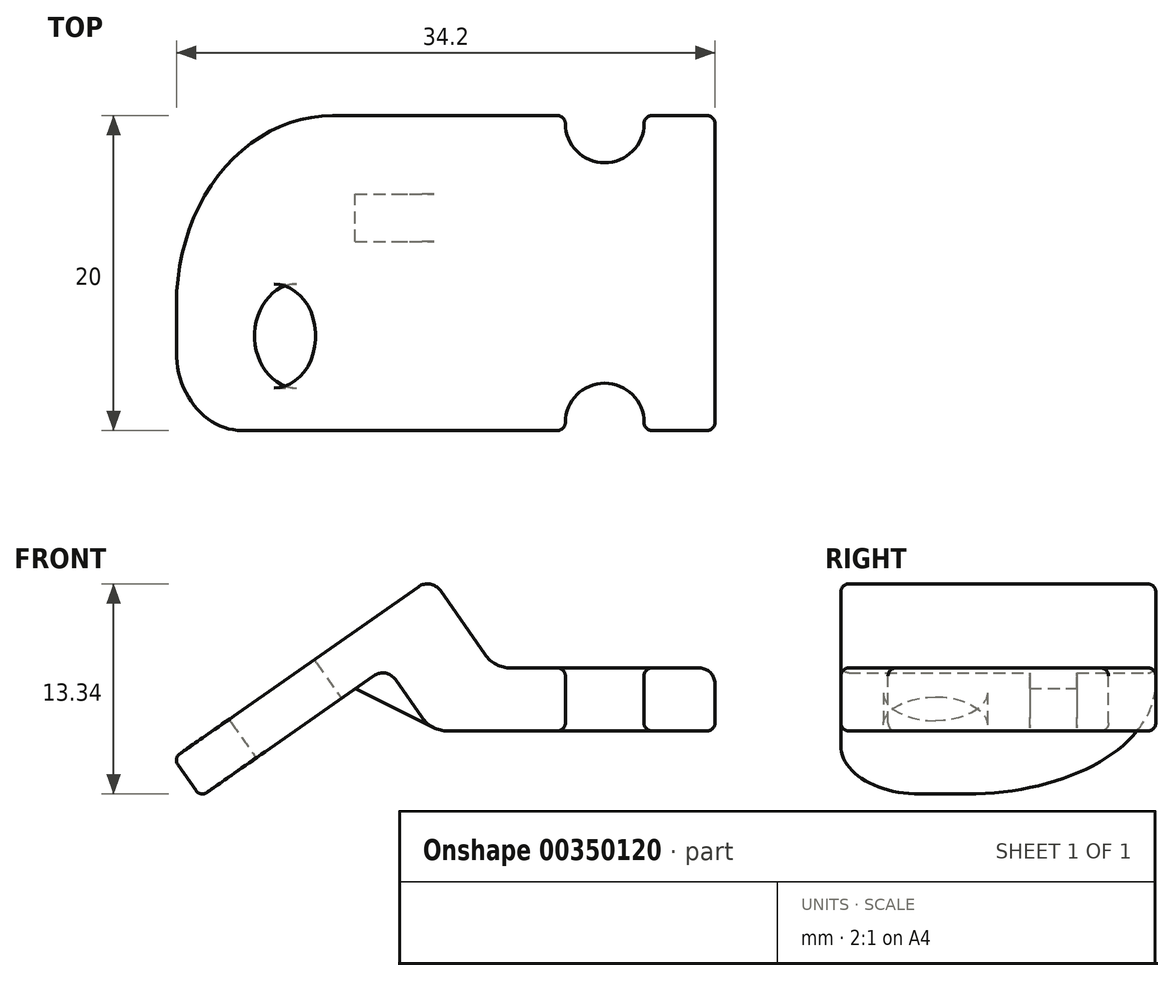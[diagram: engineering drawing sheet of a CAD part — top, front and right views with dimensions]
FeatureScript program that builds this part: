
annotation { "Feature Type Name" : "Feature", "Feature Type Description" : "" }
export const myFeature = defineFeature(function(context is Context, id is Id, definition is map)
    precondition{}
    {
        {
            var Q0;
            Q0=qCreatedBy(makeId("Front.planeOp"),FACE);
            var sketch = newSketch(context, id + "F0", { "sketchPlane" : qUnion([Q0])});
            skLineSegment(sketch, "E0", {"start": v(-18, 0) * mm, "end": v(0, 0) * mm});
            skLineSegment(sketch, "E1", {"start": v(0, 0) * mm, "end": v(0, 4) * mm});
            skLineSegment(sketch, "E2", {"start": v(0, 4) * mm, "end": v(-14, 4) * mm});
            skLineSegment(sketch, "E3", {"start": v(-14, 4) * mm, "end": v(-18.02, 9.73) * mm});
            skLineSegment(sketch, "E4", {"start": v(-18.02, 9.73) * mm, "end": v(-34.4, -1.74) * mm});
            skLineSegment(sketch, "E5", {"start": v(-34.4, -1.74) * mm, "end": v(-32.68, -4.2) * mm});
            skLineSegment(sketch, "E6", {"start": v(-32.68, -4.2) * mm, "end": v(-20.86, 4.08) * mm});
            skLineSegment(sketch, "E7", {"start": v(-18, 0) * mm, "end": v(-20.86, 4.08) * mm});
            skSolve(sketch);
        }
        {
            var Q0;
            Q0 = qSketchRegion(id + "F0", true);
            extrude(context, id + "F1", {"entities" : qUnion([Q0]), "depth" : 20 * mm});
        }
        {
            var Q0;
            Q0=makeQuery(id+"F1.opExtrude","SWEPT_FACE",FACE,{"disambiguationData":[OSD([sQuery(id+"F0.wireOp",EDGE,"E2")])]});
            var sketch = newSketch(context, id + "F2", { "sketchPlane" : qUnion([Q0])});
            skCircle(sketch, "E8", {"center": v(-7, -0.5) * mm, "radius": 2.5 * mm});
            skCircle(sketch, "E9", {"center": v(-7, -19.5) * mm, "radius": 2.5 * mm});
            skLineSegment(sketch, "E10", {"start": v(-14, -10) * mm, "end": v(0, -10) * mm, "construction": true});
            skLineSegment(sketch, "E11", {"start": v(-7, -10) * mm, "end": v(-7, -0.5) * mm, "construction": true});
            skLineSegment(sketch, "E12", {"start": v(-7, -10) * mm, "end": v(-7, -19.5) * mm, "construction": true});
            skSolve(sketch);
        }
        {
            var Q0;
            Q0 = qSketchRegion(id + "F2", true);
            extrude(context, id + "F3", {"entities" : qUnion([Q0]), "operationType" : NewBodyOperationType.REMOVE, "endBound" : BoundingType.THROUGH_ALL, "oppositeDirection" : true, "depth" : 25.4 * mm});
        }
        {
            var Q0;
            Q0=makeQuery(id+"F1.opExtrude","SWEPT_EDGE",EDGE,{"disambiguationData":[OSD([sQuery(id+"F0.wireOp",EDGE,"E6"),sQuery(id+"F0.wireOp",EDGE,"E7")])]});
            fillet(context, id + "F4", {"entities" : qUnion([Q0]), "radius" : 1 * mm, "tangentPropagation" : true, "allowEdgeOverflow" : false});
        }
        {
            var Q0;
            Q0=makeQuery(id+"F1.opExtrude","SWEPT_FACE",FACE,{"disambiguationData":[OSD([sQuery(id+"F0.wireOp",EDGE,"E6")])]});
            var sketch = newSketch(context, id + "F5", { "sketchPlane" : qUnion([Q0])});
            skLineSegment(sketch, "E13", {"start": v(-15.74, 14) * mm, "end": v(-29.17, 14) * mm, "construction": true});
            skCircle(sketch, "E14", {"center": v(-21.55, 14) * mm, "radius": 3.3 * mm});
            skSolve(sketch);
        }
        {
            var Q0;
            Q0 = qSketchRegion(id + "F5", true);
            extrude(context, id + "F6", {"entities" : qUnion([Q0]), "operationType" : NewBodyOperationType.REMOVE, "endBound" : BoundingType.THROUGH_ALL, "oppositeDirection" : true, "depth" : 25.4 * mm});
        }
        {
            var Q0;
            Q0=makeQuery(id+"F1.opExtrude","CAP_EDGE",EDGE,{"disambiguationData":[OSD([sQuery(id+"F0.wireOp",EDGE,"E5")])],"isStart":true});
            fillet(context, id + "F7", {"entities" : qUnion([Q0]), "radius" : 12 * mm, "tangentPropagation" : true, "allowEdgeOverflow" : false});
        }
        {
            var Q0;
            Q0=makeQuery(id+"F1.opExtrude","CAP_EDGE",EDGE,{"disambiguationData":[OSD([sQuery(id+"F0.wireOp",EDGE,"E5")])],"isStart":false});
            fillet(context, id + "F8", {"entities" : qUnion([Q0]), "radius" : 5 * mm, "tangentPropagation" : true, "allowEdgeOverflow" : false});
        }
        {
            var Q0;
            Q0=makeQuery(id+"F1.opExtrude","SWEPT_EDGE",EDGE,{"disambiguationData":[OSD([sQuery(id+"F0.wireOp",EDGE,"E3"),sQuery(id+"F0.wireOp",EDGE,"E4")])]});
            fillet(context, id + "F9", {"entities" : qUnion([Q0]), "radius" : 1 * mm, "tangentPropagation" : true, "allowEdgeOverflow" : false});
        }
        {
            var Q0;
            Q0=makeQuery(id+"F1.opExtrude","SWEPT_EDGE",EDGE,{"disambiguationData":[OSD([sQuery(id+"F0.wireOp",EDGE,"E2"),sQuery(id+"F0.wireOp",EDGE,"E3")])]});
            fillet(context, id + "F10", {"entities" : qUnion([Q0]), "radius" : 2 * mm, "tangentPropagation" : true, "allowEdgeOverflow" : false});
        }
        {
            var Q0;
            Q0=makeQuery(id+"F1.opExtrude","SWEPT_EDGE",EDGE,{"disambiguationData":[OSD([sQuery(id+"F0.wireOp",EDGE,"E0"),sQuery(id+"F0.wireOp",EDGE,"E7")])]});
            fillet(context, id + "F11", {"entities" : qUnion([Q0]), "radius" : 2 * mm, "tangentPropagation" : true, "allowEdgeOverflow" : false});
        }
        {
            var Q0;
            Q0=makeQuery(id+"F1.opExtrude","SWEPT_EDGE",EDGE,{"disambiguationData":[OSD([sQuery(id+"F0.wireOp",EDGE,"E1"),sQuery(id+"F0.wireOp",EDGE,"E2")])]});
            fillet(context, id + "F12", {"entities" : qUnion([Q0]), "radius" : 1 * mm, "tangentPropagation" : true, "allowEdgeOverflow" : false});
        }
        {
            var Q0;
            {var subQ0=sQuery(id+"F0.wireOp",EDGE,"E4");var subQ1=sQuery(id+"F0.wireOp",EDGE,"E2");var subQ2=sQuery(id+"F0.wireOp",EDGE,"E3");var subQ3=sQuery(id+"F0.wireOp",EDGE,"E0");var subQ4=sQuery(id+"F0.wireOp",EDGE,"E5");var subQ5=sQuery(id+"F0.wireOp",EDGE,"E6");var subQ6=sQuery(id+"F0.wireOp",EDGE,"E7");Q0=makeQuery(id+"F3.boolean.opBoolean","SPLIT",FACE,{"disambiguationData":[TD([makeQuery(id+"F1.opExtrude","SWEPT_FACE",FACE,{"disambiguationData":[OSD([subQ2])]})])],"derivedFrom":makeQuery(id+"F1.opExtrude","CAP_FACE",FACE,{"disambiguationData":[OSD([subQ3,sQuery(id+"F0.wireOp",EDGE,"E1"),subQ1,subQ2,subQ0,subQ4,subQ5,subQ6])],"isStart":true})});}
            var Q1;
            {var subQ0=sQuery(id+"F0.wireOp",EDGE,"E0");var subQ1=sQuery(id+"F0.wireOp",EDGE,"E1");var subQ2=sQuery(id+"F0.wireOp",EDGE,"E2");Q1=makeQuery(id+"F3.boolean.opBoolean","SPLIT",FACE,{"disambiguationData":[TD([makeQuery(id+"F1.opExtrude","SWEPT_FACE",FACE,{"disambiguationData":[OSD([subQ1])]})])],"derivedFrom":makeQuery(id+"F1.opExtrude","CAP_FACE",FACE,{"disambiguationData":[OSD([subQ0,subQ1,subQ2,sQuery(id+"F0.wireOp",EDGE,"E3"),sQuery(id+"F0.wireOp",EDGE,"E4"),sQuery(id+"F0.wireOp",EDGE,"E5"),sQuery(id+"F0.wireOp",EDGE,"E6"),sQuery(id+"F0.wireOp",EDGE,"E7")])],"isStart":true})});}
            var Q2;
            Q2=makeQuery(id+"F7.opFillet","BLEND_FACE",FACE,{"disambiguationData":[OSD([sQuery(id+"F0.wireOp",EDGE,"E5")])]});
            var Q3;
            Q3=makeQuery(id+"F1.opExtrude","SWEPT_FACE",FACE,{"disambiguationData":[OSD([sQuery(id+"F0.wireOp",EDGE,"E5")])]});
            var Q4;
            Q4=makeQuery(id+"F8.opFillet","BLEND_FACE",FACE,{"disambiguationData":[OSD([sQuery(id+"F0.wireOp",EDGE,"E5")])]});
            var Q5;
            {var subQ0=sQuery(id+"F0.wireOp",EDGE,"E4");var subQ1=sQuery(id+"F0.wireOp",EDGE,"E2");var subQ2=sQuery(id+"F0.wireOp",EDGE,"E3");var subQ3=sQuery(id+"F0.wireOp",EDGE,"E0");var subQ4=sQuery(id+"F0.wireOp",EDGE,"E5");var subQ5=sQuery(id+"F0.wireOp",EDGE,"E6");var subQ6=sQuery(id+"F0.wireOp",EDGE,"E7");Q5=makeQuery(id+"F3.boolean.opBoolean","SPLIT",FACE,{"disambiguationData":[TD([makeQuery(id+"F1.opExtrude","SWEPT_FACE",FACE,{"disambiguationData":[OSD([subQ2])]})])],"derivedFrom":makeQuery(id+"F1.opExtrude","CAP_FACE",FACE,{"disambiguationData":[OSD([subQ3,sQuery(id+"F0.wireOp",EDGE,"E1"),subQ1,subQ2,subQ0,subQ4,subQ5,subQ6])],"isStart":false})});}
            var Q6;
            {var subQ0=sQuery(id+"F0.wireOp",EDGE,"E0");var subQ1=sQuery(id+"F0.wireOp",EDGE,"E1");var subQ2=sQuery(id+"F0.wireOp",EDGE,"E2");Q6=makeQuery(id+"F3.boolean.opBoolean","SPLIT",FACE,{"disambiguationData":[TD([makeQuery(id+"F1.opExtrude","SWEPT_FACE",FACE,{"disambiguationData":[OSD([subQ1])]})])],"derivedFrom":makeQuery(id+"F1.opExtrude","CAP_FACE",FACE,{"disambiguationData":[OSD([subQ0,subQ1,subQ2,sQuery(id+"F0.wireOp",EDGE,"E3"),sQuery(id+"F0.wireOp",EDGE,"E4"),sQuery(id+"F0.wireOp",EDGE,"E5"),sQuery(id+"F0.wireOp",EDGE,"E6"),sQuery(id+"F0.wireOp",EDGE,"E7")])],"isStart":false})});}
            var Q7;
            Q7=makeQuery(id+"F3.boolean.opBoolean","COPY",FACE,{"derivedFrom":makeQuery(id+"F3.opExtrude","SWEPT_FACE",FACE,{"disambiguationData":[OSD([sQuery(id+"F2.wireOp",EDGE,"E9")])]})});
            var Q8;
            Q8=makeQuery(id+"F3.boolean.opBoolean","COPY",FACE,{"derivedFrom":makeQuery(id+"F3.opExtrude","SWEPT_FACE",FACE,{"disambiguationData":[OSD([sQuery(id+"F2.wireOp",EDGE,"E8")])]})});
            var Q9;
            Q9=makeQuery(id+"F1.opExtrude","SWEPT_FACE",FACE,{"disambiguationData":[OSD([sQuery(id+"F0.wireOp",EDGE,"E1")])]});
            fillet(context, id + "F13", {"entities" : qUnion([Q0, Q1, Q2, Q3, Q4, Q5, Q6, Q7, Q8, Q9]), "radius" : .5 * mm, "tangentPropagation" : true, "allowEdgeOverflow" : false});
        }
        {
            var Q0;
            {var subQ0=sQuery(id+"F0.wireOp",EDGE,"E4");var subQ1=sQuery(id+"F0.wireOp",EDGE,"E2");var subQ2=sQuery(id+"F0.wireOp",EDGE,"E3");var subQ3=sQuery(id+"F0.wireOp",EDGE,"E0");var subQ4=sQuery(id+"F0.wireOp",EDGE,"E5");var subQ5=sQuery(id+"F0.wireOp",EDGE,"E6");var subQ6=sQuery(id+"F0.wireOp",EDGE,"E7");Q0=makeQuery(id+"F3.boolean.opBoolean","SPLIT",FACE,{"disambiguationData":[TD([makeQuery(id+"F1.opExtrude","SWEPT_FACE",FACE,{"disambiguationData":[OSD([subQ2])]})])],"derivedFrom":makeQuery(id+"F1.opExtrude","CAP_FACE",FACE,{"disambiguationData":[OSD([subQ3,sQuery(id+"F0.wireOp",EDGE,"E1"),subQ1,subQ2,subQ0,subQ4,subQ5,subQ6])],"isStart":true})});}
            cPlane(context, id + "F14", {"entities" : qUnion([Q0]), "cplaneType" : CPlaneType.OFFSET, "offset" : 5 * mm, "oppositeDirection" : true, "width" : 152.4 * mm, "height" : 152.4 * mm});
        }
        {
            var Q0;
            Q0=qCreatedBy(id+"F14.planeOp",FACE);
            var sketch = newSketch(context, id + "F15", { "sketchPlane" : qUnion([Q0])});
            skArc(sketch, "E15.0", {"start": v(18.6, 0.85) * mm, "mid": v(18.1, 0.36) * mm, "end": v(17.47, 0.07) * mm});
            skLineSegment(sketch, "E16.0", {"start": v(20.28, 3.26) * mm, "end": v(18.6, 0.85) * mm});
            skArc(sketch, "E17.0", {"start": v(21.68, 3.5) * mm, "mid": v(20.93, 3.67) * mm, "end": v(20.28, 3.26) * mm});
            skLineSegment(sketch, "E18.0", {"start": v(22.85, 2.69) * mm, "end": v(21.68, 3.5) * mm});
            skLineSegment(sketch, "E19", {"start": v(22.85, 2.69) * mm, "end": v(17.47, 0.02) * mm});
            skPoint(sketch, "E19.endSnap0", {"position": v(17.47, 0.07) * mm});
            skPoint(sketch, "E20.orphan", {"position": v(16.96, 0) * mm});
            skSolve(sketch);
        }
        {
            var Q0;
            Q0 = qSketchRegion(id + "F15", true);
            extrude(context, id + "F16", {"entities" : qUnion([Q0]), "operationType" : NewBodyOperationType.ADD, "oppositeDirection" : true, "depth" : 3 * mm});
        }
        {
            var Q0;
            Q0=makeQuery(id+"F6.boolean.opBoolean","COPY",FACE,{"derivedFrom":makeQuery(id+"F6.opExtrude","SWEPT_FACE",FACE,{"disambiguationData":[OSD([sQuery(id+"F5.wireOp",EDGE,"E14")])]})});
            fillet(context, id + "F17", {"entities" : qUnion([Q0]), "radius" : .25 * mm, "tangentPropagation" : true, "allowEdgeOverflow" : false});
        }
    });
